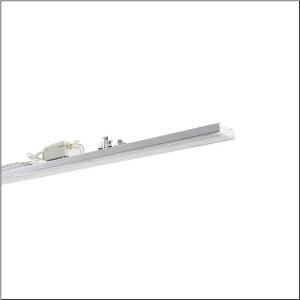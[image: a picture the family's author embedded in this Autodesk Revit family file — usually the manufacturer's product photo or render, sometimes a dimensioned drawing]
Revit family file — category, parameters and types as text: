
# Revit family: licross_11_recessed_ho_51tl12mn46xm
name_source: partatom
category: Lighting Fixtures
units: mm (PartAtom-declared; Revit-internal decimal feet)

## family parameters
Cut with Voids When Loaded = No
Host = Face
Light Source = No
Part Type = Normal
Room Calculation Point = No
Round Connector Dimension = Use Diameter
Shared = No

## types (1)
- --- (1 x LED, 6020 lm, 30.1 W, 4000K)
    Apparent Load = 30 VA
    CIE Flux Codes = 66 91 98 100 100
    Color Rendering = 80
    Color Temperature = 4000K
    Default Elevation = 1800 mm
    Description = Licross 11 Recessed HO, luminaire insert, of sheet steel, coil coated, white, length: 1.500mm, width: 66mm, height: 67mm, LED rated luminous flux: 6.020lm, light colour: 840, SDCM (Standard Deviation of Colour Matching)MacAdam ≤ 2 SDCM (initial), control gear: ON/OFF Multilumen, with plug, 3-pole, with phase selection, mains connection: 220..240V, AC, 50/60Hz, rated input power: 30W, internal wiring halogen-free, primary optical cover: cover, of PMMA, light emission: direct distribution, primary light characteristic: symmetric, protection rating (complete): IP40, insulation class (complete): insulation class I (protective earthing), certification: CE, ENEC, VDE, UKCA, protection symbol: D if used in an environment without relevant dust loads with corresponding accessories, impact resistance: IK06, permissible ambient temperature for indoor applications: -35..+50°C, corresponds to IFS (International Featured Standards) requirements for safety and quality in the food industry, reducing of maximum allowable ambient temperature of 5°C with ceiling mounting, The light source and the operating device comply with the requirements of the Ecodesign Regulation (EU) 2019/2020 and are replaceable in accordance with this regulation, packaging unit: 1 piece
    Height = 58 mm
    Lamp = 1 x LED
    Lamp Light Flux = 6020 lm
    Lamp Power = 30.1 W
    Lamp count = 1
    Length = 1500 mm
    Luminous efficacy = 200 lm/W
    Manufacturer = Siteco
    ModVariant = No
    Model = 51TL12MN46XM
    Mounting Place = Ceiling
    Mounting Type = Pendant
    Number of Poles = 1
    OnlyDefault = Yes
    Power Factor = 1
    Product Name = Licross 11 Recessed HO
    Product group = luminaire insert | ceiling pendant
    ProductGroupID = 901
    Protection Class = Protection class I
    Protection Degree = IP 40
    RLX_Detail_Level = 1
    RLX_Emergency_Light_Flux = 0 lm
    RLX_Emergency_Type = 0
    RLX_Emergency_Type_DB = No
    RlxData = <blob elided: 22333 chars, md5=ea35e541>
    Socket = socket
    Standby Power = 0 W
    System Light Flux = 6020 lm
    System Power = 30 W
    Type Comments = factory setting: luminous flux: 100 % | (A | C | E) | 71 mA
    Type Image = l_1296930.jpg
    URL = http://relux.com
    VarID = @adj_091155
    Voltage = 0 V
    Weight = 0.00 kg
    Width = 66 mm

## geometry (parser evidence)
native form markers: Blend x4, Sweep x10
no freeform markers — native parametric forms only
